# Revit family: Воздушная завеса с эл. подогревом TVP-E
name_source: partatom
category: Оборудование
revit_build: Autodesk Revit 2017 (Build: 20161006_0315(x64)
units: mm (PartAtom-declared; Revit-internal decimal feet)

## family parameters
Всегда вертикально = Да
На основе рабочей плоскости = Нет
Общий = Нет
При загрузке вырезать с полостями = Нет
Размер круглого соединителя = Использовать диаметр
Тип детали = Нормальный
Точка расчета площади = Нет

## types (6) — shared parameters
Единица измерения = шт.
Завод изготовитель = ООО "ЮНИО-ВЕНТ"
И1 = 2000 мм
Ключевая пометка = Вентиляция
Материал = Сталь серая
Наименование и тех.хар-ка = Воздушная завеса с электрическим подогревом
Напряжение U,В = 3-380
Раздел = ОВ
Ширина щели = 42 мм
отступ = 50 мм
х2 = 1000 мм

## per-type parameters (varying)
| type | А | Б | Б1 | Высота | И2 | Мощность двигателя N,Вт | Мощность, кВт | Сила тока J, А | Тип, марка, обозначение | Ток эл. нагревателя, А | Ширина | х | х1 |
| 60-30 | 600 мм | 300 мм | 90 мм | 300 мм | 1502 мм | 1100 | 15 Вт | 2.5 | ЗВП-Е 60-30 | 22,6 | 600 мм | 1051 мм | 631 мм |
| 60-35 | 600 мм | 350 мм | 105 мм | 350 мм | 1622 мм | 1500 | 23 Вт | 3.3 | ЗВП-Е 60-35 | 33.9 | 600 мм | 1135 мм | 681 мм |
| 70-40 M | 700 мм | 400 мм | 120 мм | 400 мм | 1602 мм | 1500 | 30 Вт | 3.3 | ЗВП-Е 70-40 M | 45.1 | 700 мм | 1121 мм | 673 мм |
| 70-40 | 700 мм | 400 мм | 120 мм | 400 мм | 1602 мм | 3 | 30 Вт | 6.1 | ЗВП-Е 70-40 | 45.1 | 700 мм | 1121 мм | 673 мм |
| 80-50 | 800 мм | 500 мм | 150 мм | 500 мм | 1727 мм | 3000 | 30 Вт | 6.1 | ЗВП-Е 80-50 | 45.1 | 800 мм | 1209 мм | 725 мм |
| 90-50 | 900 мм | 500 мм | 150 мм | 500 мм | 2003 мм | 5500 | 45 Вт | 10.9 | ЗВП-Е 90-50 | 67.6 | 900 мм | 1402 мм | 841 мм |
